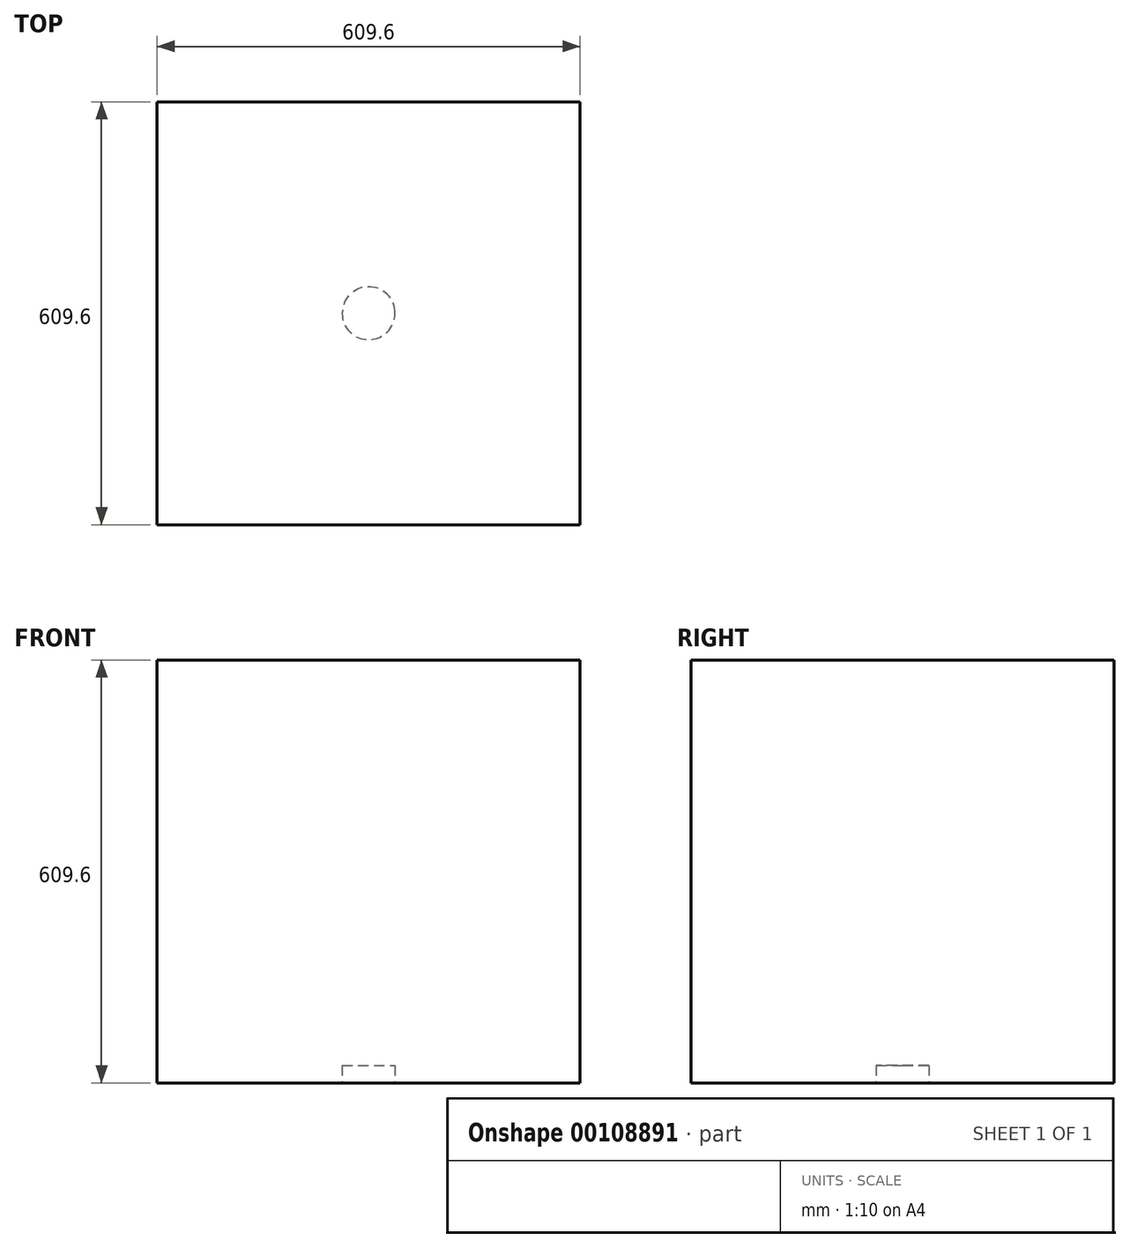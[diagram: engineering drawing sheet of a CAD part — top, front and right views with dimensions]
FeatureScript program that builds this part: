
annotation { "Feature Type Name" : "Feature", "Feature Type Description" : "" }
export const myFeature = defineFeature(function(context is Context, id is Id, definition is map)
    precondition{}
    {
        {
            var Q0;
            Q0=qCreatedBy(makeId("Front.planeOp"),FACE);
            var sketch = newSketch(context, id + "F0", { "sketchPlane" : qUnion([Q0])});
            skLineSegment(sketch, "E0.bottom", {"start": v(-304.8, 0) * mm, "end": v(304.8, 0) * mm});
            skLineSegment(sketch, "E0.top", {"start": v(-304.8, -609.6) * mm, "end": v(304.8, -609.6) * mm});
            skLineSegment(sketch, "E0.left", {"start": v(-304.8, 0) * mm, "end": v(-304.8, -609.6) * mm});
            skLineSegment(sketch, "E0.right", {"start": v(304.8, 0) * mm, "end": v(304.8, -609.6) * mm});
            skSolve(sketch);
        }
        {
            var Q0;
            Q0 = qSketchRegion(id + "F0", true);
            extrude(context, id + "F1", {"entities" : qUnion([Q0]), "endBound" : BoundingType.SYMMETRIC, "depth" : 609.6 * mm});
        }
        {
            var Q0;
            Q0=makeQuery(id+"F1.opExtrude","SWEPT_FACE",FACE,{"disambiguationData":[OSD([sQuery(id+"F0.wireOp",EDGE,"E0.top")])]});
            var sketch = newSketch(context, id + "F2", { "sketchPlane" : qUnion([Q0])});
            skCircle(sketch, "E1", {"center": v(0, 0) * mm, "radius": 38.1 * mm});
            skSolve(sketch);
        }
        {
            var Q0;
            Q0 = qSketchRegion(id + "F2", true);
            extrude(context, id + "F3", {"entities" : qUnion([Q0]), "operationType" : NewBodyOperationType.REMOVE, "oppositeDirection" : true, "depth" : 25.4 * mm});
        }
    });
